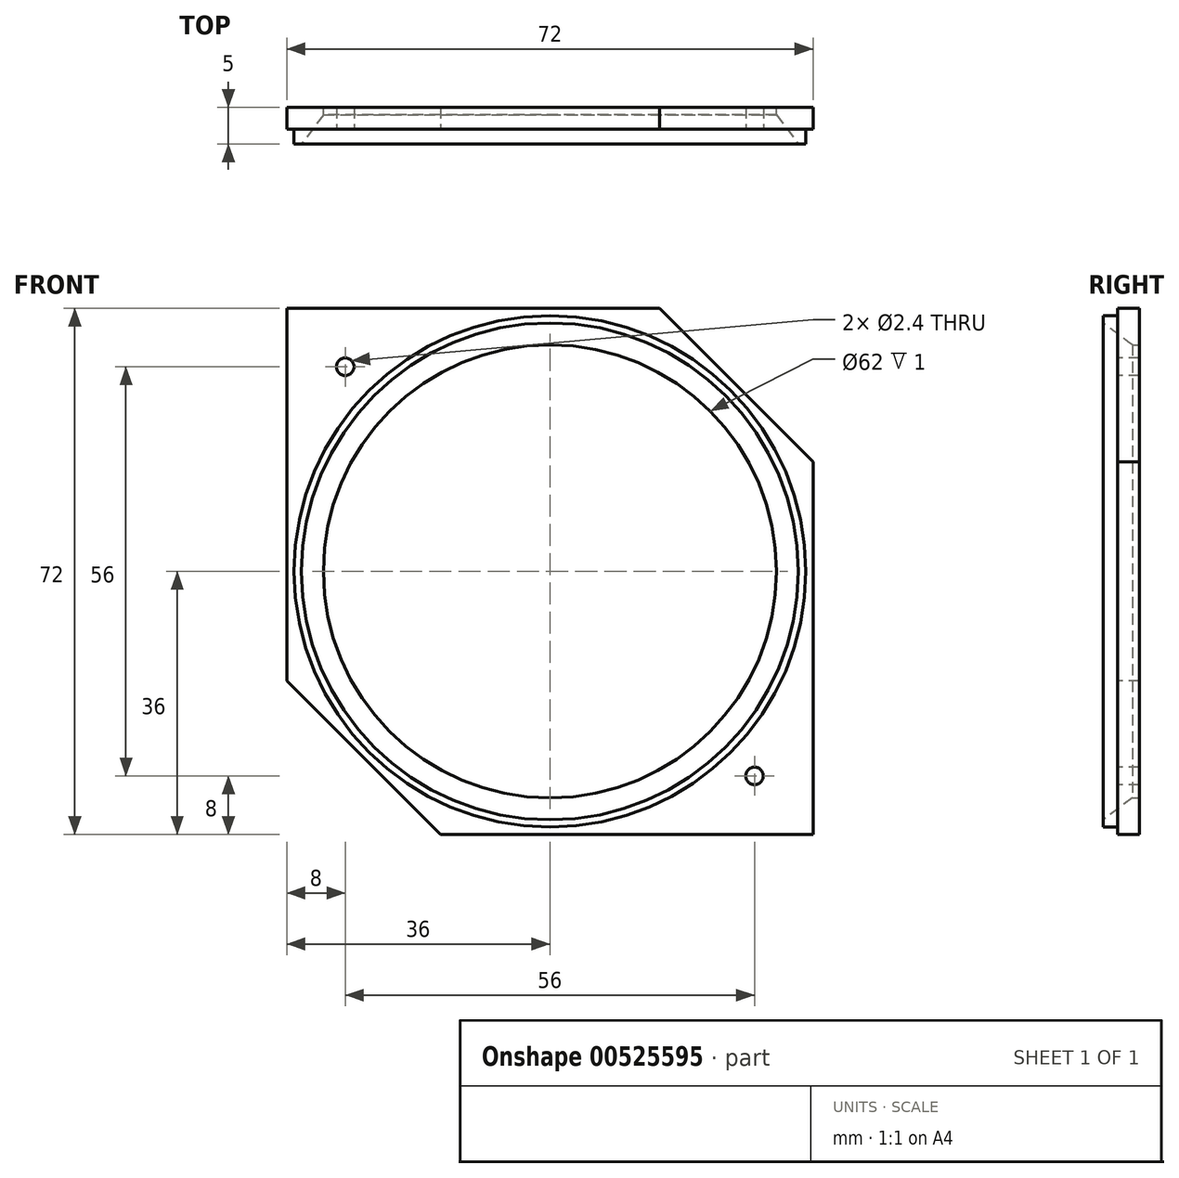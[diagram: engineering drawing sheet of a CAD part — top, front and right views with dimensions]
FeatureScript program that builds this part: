
annotation { "Feature Type Name" : "Feature", "Feature Type Description" : "" }
export const myFeature = defineFeature(function(context is Context, id is Id, definition is map)
    precondition{}
    {
        {
            var Q0;
            Q0=qCreatedBy(makeId("Right.planeOp"),FACE);
            var sketch = newSketch(context, id + "F0", { "sketchPlane" : qUnion([Q0])});
            skLineSegment(sketch, "E0", {"start": v(19.32, 0) * mm, "end": v(-16.11, 0) * mm, "construction": true});
            skLineSegment(sketch, "E1", {"start": v(-3, 35) * mm, "end": v(-3, 34) * mm});
            skLineSegment(sketch, "E2", {"start": v(2, 31) * mm, "end": v(2, 35) * mm});
            skLineSegment(sketch, "E3", {"start": v(2, 35) * mm, "end": v(-3, 35) * mm});
            skLineSegment(sketch, "E4", {"start": v(2, 31) * mm, "end": v(1, 31) * mm});
            skLineSegment(sketch, "E5", {"start": v(1, 31) * mm, "end": v(-3, 34) * mm});
            skSolve(sketch);
        }
        {
            var Q0;
            Q0=qSketchRegion(id+"F0",true);
            var Q1;
            Q1=sQuery(id+"F0.wireOp",EDGE,"E0");
            revolve(context, id + "F1", {"entities" : qUnion([Q0]), "axis" : qUnion([Q1]), "revolveType" : RevolveType.FULL});
        }
        {
            var Q0;
            Q0=makeQuery(id+"F1.opRevolve","SWEPT_FACE",FACE,{"disambiguationData":[OSD([sQuery(id+"F0.wireOp",EDGE,"E1")])]});
            cPlane(context, id + "F2", {"entities" : qUnion([Q0]), "cplaneType" : CPlaneType.OFFSET, "offset" : 2 * mm, "oppositeDirection" : true, "width" : 150 * mm, "height" : 150 * mm});
        }
        {
            var Q0;
            Q0=qCreatedBy(id+"F2.planeOp",FACE);
            var sketch = newSketch(context, id + "F3", { "sketchPlane" : qUnion([Q0])});
            skPoint(sketch, "E6.middle", {"position": v(0, 0) * mm});
            skCircle(sketch, "E7", {"center": v(-28, 28) * mm, "radius": 1.2 * mm});
            skCircle(sketch, "E8", {"center": v(-28, -28) * mm, "radius": 1.2 * mm, "construction": true});
            skCircle(sketch, "E9", {"center": v(28, -28) * mm, "radius": 1.2 * mm});
            skCircle(sketch, "E10", {"center": v(28, 28) * mm, "radius": 1.2 * mm, "construction": true});
            skCircle(sketch, "E11", {"center": v(0, 0) * mm, "radius": 35 * mm});
            skLineSegment(sketch, "E12.bottom", {"start": v(36, -36) * mm, "end": v(-15, -36) * mm});
            skLineSegment(sketch, "E12.right", {"start": v(-36, -15) * mm, "end": v(-36, 36) * mm});
            skLineSegment(sketch, "E13", {"start": v(-36, -15) * mm, "end": v(-15, -36) * mm});
            skLineSegment(sketch, "E14", {"start": v(0, 0) * mm, "end": v(17.48, 0) * mm, "construction": true});
            skLineSegment(sketch, "E15", {"start": v(0, 0) * mm, "end": v(0, 7) * mm, "construction": true});
            skLineSegment(sketch, "E16", {"start": v(19.95, -19.95) * mm, "end": v(0, 0) * mm, "construction": true});
            skLineSegment(sketch, "E17", {"start": v(15, 36) * mm, "end": v(36, 15) * mm});
            skLineSegment(sketch, "E18", {"start": v(-36, 36) * mm, "end": v(15, 36) * mm});
            skLineSegment(sketch, "E19", {"start": v(36, -36) * mm, "end": v(36, 15) * mm});
            skSolve(sketch);
        }
        {
            var Q0;
            Q0=qSketchRegion(id+"F3",true);
            extrude(context, id + "F4", {"entities" : qUnion([Q0]), "operationType" : NewBodyOperationType.ADD, "oppositeDirection" : true, "depth" : 3 * mm, "offsetDistance" : 25 * mm});
        }
    });
